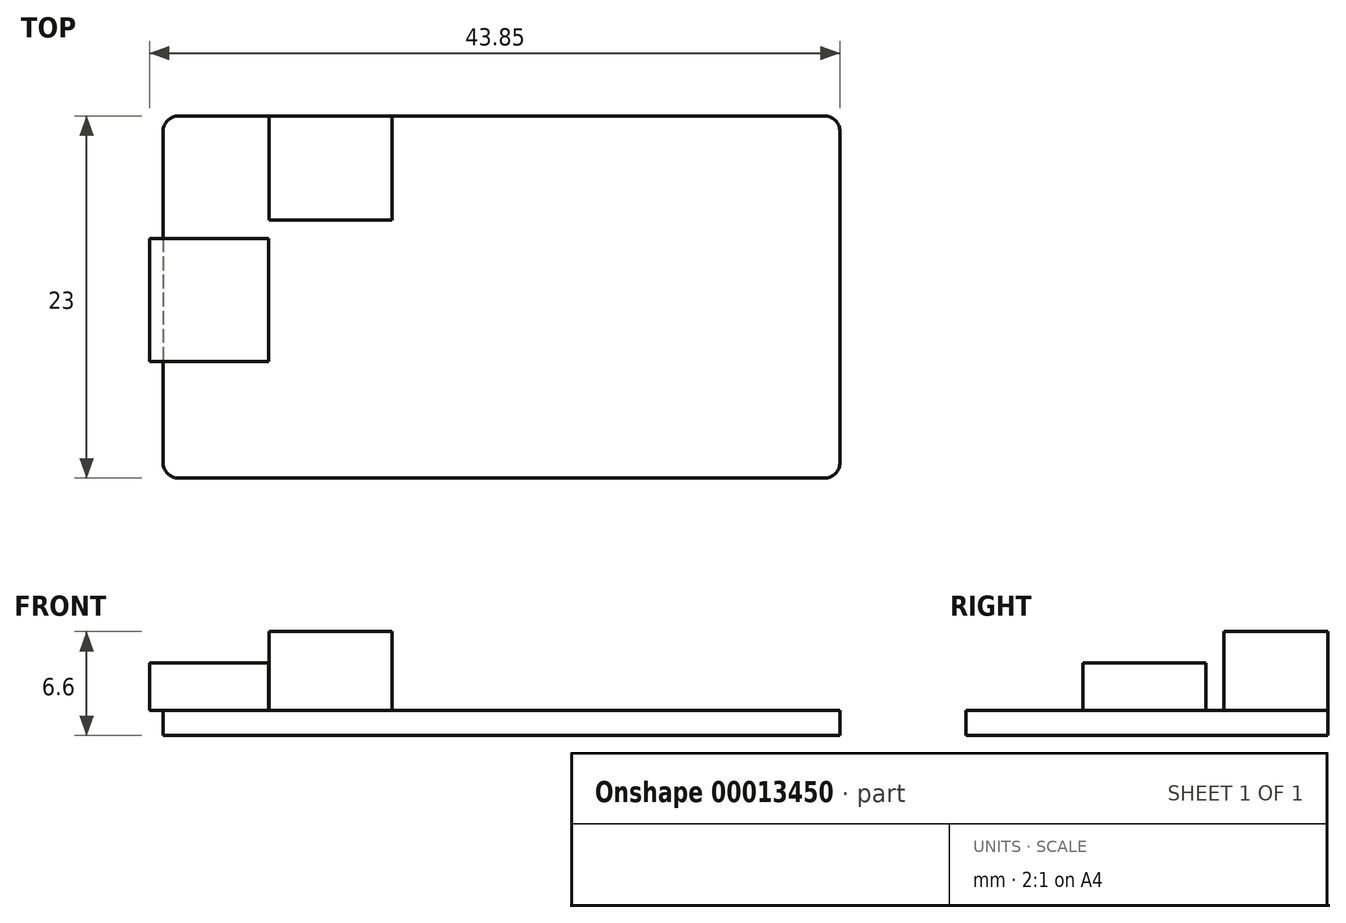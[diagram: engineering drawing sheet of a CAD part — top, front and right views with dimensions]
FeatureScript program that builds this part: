
annotation { "Feature Type Name" : "Feature", "Feature Type Description" : "" }
export const myFeature = defineFeature(function(context is Context, id is Id, definition is map)
    precondition{}
    {
        {
            var Q0;
            Q0=qCreatedBy(makeId("Top.planeOp"),FACE);
            var sketch = newSketch(context, id + "F0", { "sketchPlane" : qUnion([Q0])});
            skLineSegment(sketch, "E0.bottom", {"start": v(-25.23, 17.9) * mm, "end": v(15.77, 17.9) * mm});
            skLineSegment(sketch, "E0.top", {"start": v(-25.23, -5.1) * mm, "end": v(15.77, -5.1) * mm});
            skLineSegment(sketch, "E0.left", {"start": v(-26.23, 16.9) * mm, "end": v(-26.23, -4.1) * mm});
            skLineSegment(sketch, "E0.right", {"start": v(16.77, 16.9) * mm, "end": v(16.77, -4.1) * mm});
            skPoint(sketch, "E1.visualSharp", {"position": v(-26.23, -5.1) * mm});
            skArc(sketch, "E1.filletArc", {"start": v(-26.23, -4.1) * mm, "mid": v(-25.94, -4.8) * mm, "end": v(-25.23, -5.1) * mm});
            skPoint(sketch, "E2.visualSharp", {"position": v(-26.23, 17.9) * mm});
            skArc(sketch, "E2.filletArc", {"start": v(-25.23, 17.9) * mm, "mid": v(-25.94, 17.62) * mm, "end": v(-26.23, 16.9) * mm});
            skPoint(sketch, "E3.visualSharp", {"position": v(16.77, -5.1) * mm});
            skArc(sketch, "E3.filletArc", {"start": v(15.77, -5.1) * mm, "mid": v(16.47, -4.8) * mm, "end": v(16.77, -4.1) * mm});
            skPoint(sketch, "E4.visualSharp", {"position": v(16.77, 17.9) * mm});
            skArc(sketch, "E4.filletArc", {"start": v(16.77, 16.9) * mm, "mid": v(16.47, 17.62) * mm, "end": v(15.77, 17.9) * mm});
            skSolve(sketch);
        }
        {
            var Q0;
            Q0=qSketchRegion(id+"F0",true);
            extrude(context, id + "F1", {"entities" : qUnion([Q0]), "depth" : 1.6 * mm});
        }
        {
            var Q0;
            Q0=makeQuery(id+"F1.opExtrude","CAP_FACE",FACE,{"disambiguationData":[OSD([sQuery(id+"F0.wireOp",EDGE,"E0.bottom"),sQuery(id+"F0.wireOp",EDGE,"E0.top"),sQuery(id+"F0.wireOp",EDGE,"E0.left"),sQuery(id+"F0.wireOp",EDGE,"E0.right")])],"isStart":false});
            var sketch = newSketch(context, id + "F2", { "sketchPlane" : qUnion([Q0])});
            skLineSegment(sketch, "E5.bottom", {"start": v(-27.08, 10.13) * mm, "end": v(-19.52, 10.13) * mm});
            skLineSegment(sketch, "E5.top", {"start": v(-27.08, 2.32) * mm, "end": v(-19.52, 2.32) * mm});
            skLineSegment(sketch, "E5.left", {"start": v(-27.08, 10.13) * mm, "end": v(-27.08, 2.32) * mm});
            skLineSegment(sketch, "E5.right", {"start": v(-19.52, 10.13) * mm, "end": v(-19.52, 2.32) * mm});
            skSolve(sketch);
        }
        {
            var Q0;
            Q0=qSketchRegion(id+"F2",true);
            extrude(context, id + "F3", {"entities" : qUnion([Q0]), "operationType" : NewBodyOperationType.ADD, "depth" : 3 * mm});
        }
        {
            var Q0;
            Q0=makeQuery(id+"F1.opExtrude","CAP_FACE",FACE,{"disambiguationData":[OSD([sQuery(id+"F0.wireOp",EDGE,"E0.bottom"),sQuery(id+"F0.wireOp",EDGE,"E0.top"),sQuery(id+"F0.wireOp",EDGE,"E0.left"),sQuery(id+"F0.wireOp",EDGE,"E0.right")])],"isStart":false});
            var sketch = newSketch(context, id + "F4", { "sketchPlane" : qUnion([Q0])});
            skLineSegment(sketch, "E6.bottom", {"start": v(-19.5, 17.9) * mm, "end": v(-11.7, 17.9) * mm});
            skLineSegment(sketch, "E6.top", {"start": v(-19.5, 11.3) * mm, "end": v(-11.7, 11.3) * mm});
            skLineSegment(sketch, "E6.left", {"start": v(-19.5, 17.9) * mm, "end": v(-19.5, 11.3) * mm});
            skLineSegment(sketch, "E6.right", {"start": v(-11.7, 17.9) * mm, "end": v(-11.7, 11.3) * mm});
            skSolve(sketch);
        }
        {
            var Q0;
            Q0=qSketchRegion(id+"F4",true);
            extrude(context, id + "F5", {"entities" : qUnion([Q0]), "operationType" : NewBodyOperationType.ADD, "depth" : 5 * mm});
        }
    });
